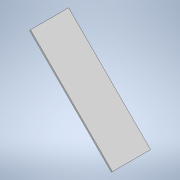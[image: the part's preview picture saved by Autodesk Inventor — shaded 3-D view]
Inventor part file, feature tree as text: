
AUTODESK INVENTOR PART (.ipt)
format: ipt  version: 2022.2 (Build 262287010, 287A)  size: 95,744 bytes
history: native  units: mm
features: other x1, plane x1, extrude x1, sketch x1
ambient origin geometry x8: Origin, YZ Plane, XZ Plane, XY Plane, X Axis, Y Axis, Z Axis, Center Point
bodies: Body1 (feature_tree)
feature tree (4):
  other  "Sólido1"
  plane  "Plano de trabajo1"
  extrude  "Extrusión3"  Depth=1.0mm TaperAngle=0.0deg
  sketch  "Boceto3"  dims[d10=25.0mm d11=76.0mm d12=1.0mm d13=0.0mm]
